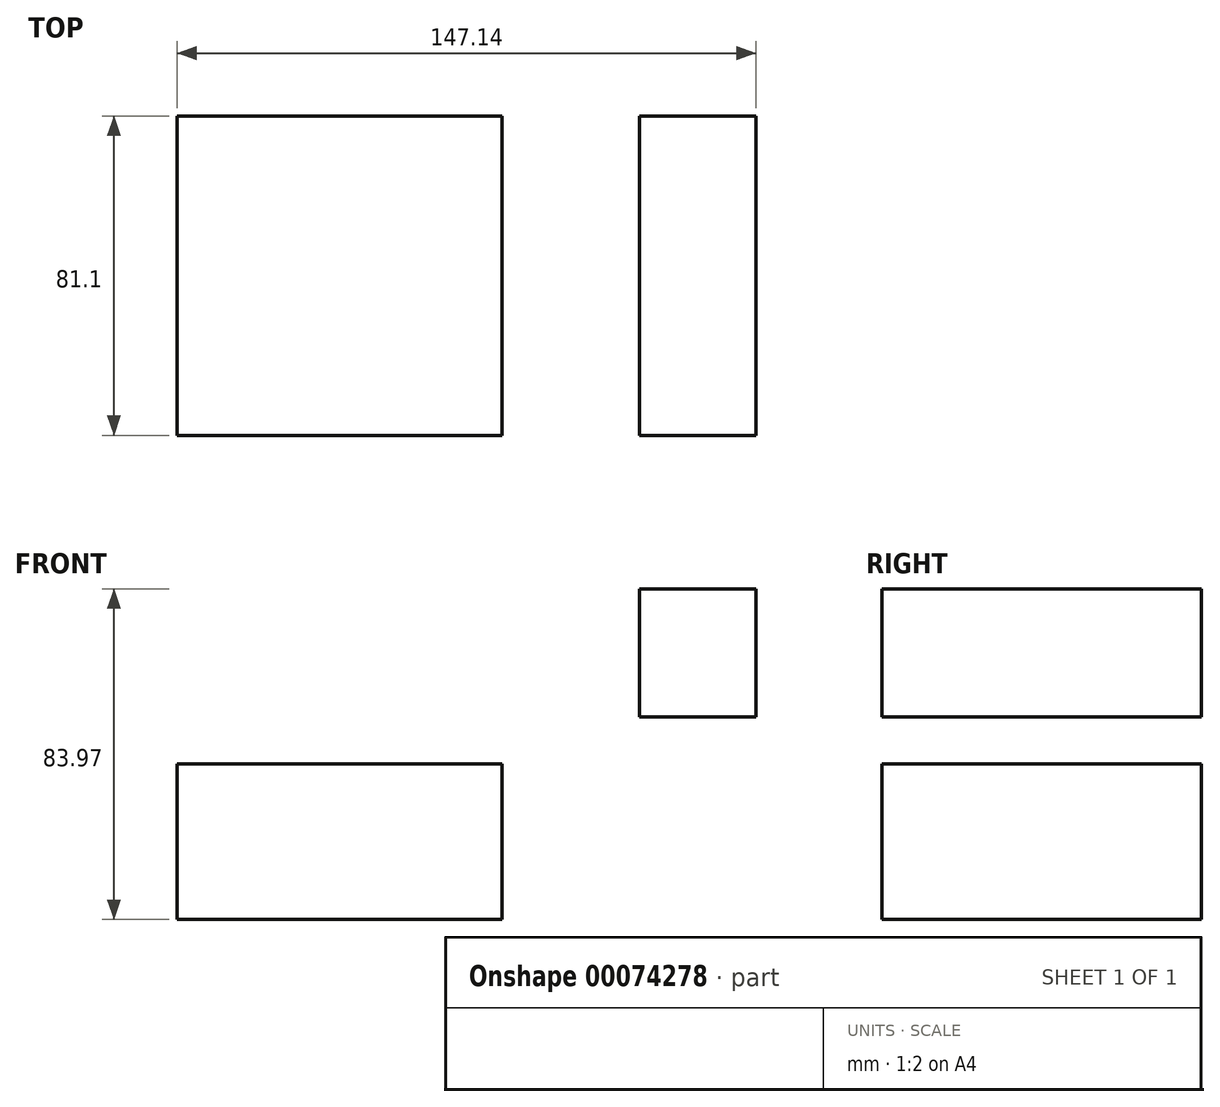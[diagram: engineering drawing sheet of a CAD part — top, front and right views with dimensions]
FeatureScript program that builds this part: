
annotation { "Feature Type Name" : "Feature", "Feature Type Description" : "" }
export const myFeature = defineFeature(function(context is Context, id is Id, definition is map)
    precondition{}
    {
        {
            var Q0;
            Q0=qCreatedBy(makeId("Front.planeOp"),FACE);
            var sketch = newSketch(context, id + "F0", { "sketchPlane" : qUnion([Q0])});
            skLineSegment(sketch, "E0.rect.bottom", {"start": v(-0.28, -52.54) * mm, "end": v(-82.83, -52.54) * mm});
            skLineSegment(sketch, "E0.rect.top", {"start": v(-0.28, -13.03) * mm, "end": v(-82.83, -13.03) * mm});
            skLineSegment(sketch, "E0.rect.left", {"start": v(-0.28, -52.54) * mm, "end": v(-0.28, -13.03) * mm});
            skLineSegment(sketch, "E0.rect.right", {"start": v(-82.83, -52.54) * mm, "end": v(-82.83, -13.03) * mm});
            skPoint(sketch, "E0.rect.middle", {"position": v(-41.56, -32.78) * mm});
            skLineSegment(sketch, "E1.rect.bottom", {"start": v(64.31, -1.16) * mm, "end": v(13.51, -1.16) * mm});
            skLineSegment(sketch, "E1.rect.top", {"start": v(64.31, 31.43) * mm, "end": v(13.51, 31.43) * mm});
            skLineSegment(sketch, "E1.rect.left", {"start": v(64.31, -1.16) * mm, "end": v(64.31, 31.43) * mm});
            skLineSegment(sketch, "E1.rect.right", {"start": v(13.51, -1.16) * mm, "end": v(13.51, 31.43) * mm});
            skPoint(sketch, "E1.rect.middle", {"position": v(38.91, 15.13) * mm});
            skLineSegment(sketch, "E2", {"start": v(-0.28, -13.03) * mm, "end": v(-0.28, 3.96) * mm});
            skArc(sketch, "E3", {"start": v(-0.28, 3.96) * mm, "mid": v(1.78, 8.47) * mm, "end": v(6.54, 9.85) * mm});
            skLineSegment(sketch, "E4", {"start": v(6.54, 9.85) * mm, "end": v(34.65, 9.85) * mm});
            skLineSegment(sketch, "E5.0", {"start": v(7.35, 25.85) * mm, "end": v(34.65, 25.85) * mm});
            skArc(sketch, "E5.1", {"start": v(-16.29, 3.96) * mm, "mid": v(-9.25, 20.07) * mm, "end": v(7.35, 25.85) * mm});
            skLineSegment(sketch, "E5.2", {"start": v(-16.29, -13.03) * mm, "end": v(-16.29, 3.96) * mm});
            skLineSegment(sketch, "E6", {"start": v(34.65, -1.16) * mm, "end": v(34.65, 31.43) * mm});
            skFitSpline(sketch, "E7", {"points": [v(-82.83, -13.03) * mm, v(13.51, 25.85) * mm], "startDerivative": vector(-4.6, 136.77) * mm, "endDerivative": vector(-0.6, -38.28) * mm});
            skSolve(sketch);
        }
        {
            var Q0;
            Q0=makeQuery(id+"F0.imprint","IMPRINT",FACE,{"disambiguationData":[TD([[makeQuery(id+"F0.imprint","IMPRINT",EDGE,{"derivedFrom":sQuery(id+"F0.wireOp",EDGE,"E0.rect.bottom")}),-1.0]])]});
            var Q1;
            {var subQ0=sQuery(id+"F0.wireOp",EDGE,"E1.rect.left");Q1=makeQuery(id+"F0.imprint","IMPRINT",FACE,{"disambiguationData":[TD([[makeQuery(id+"F0.imprint","IMPRINT",EDGE,{"derivedFrom":subQ0}),1.0]])]});}
            extrude(context, id + "F1", {"entities" : qUnion([Q0, Q1]), "oppositeDirection" : true, "depth" : 81.1 * mm});
        }
    });
